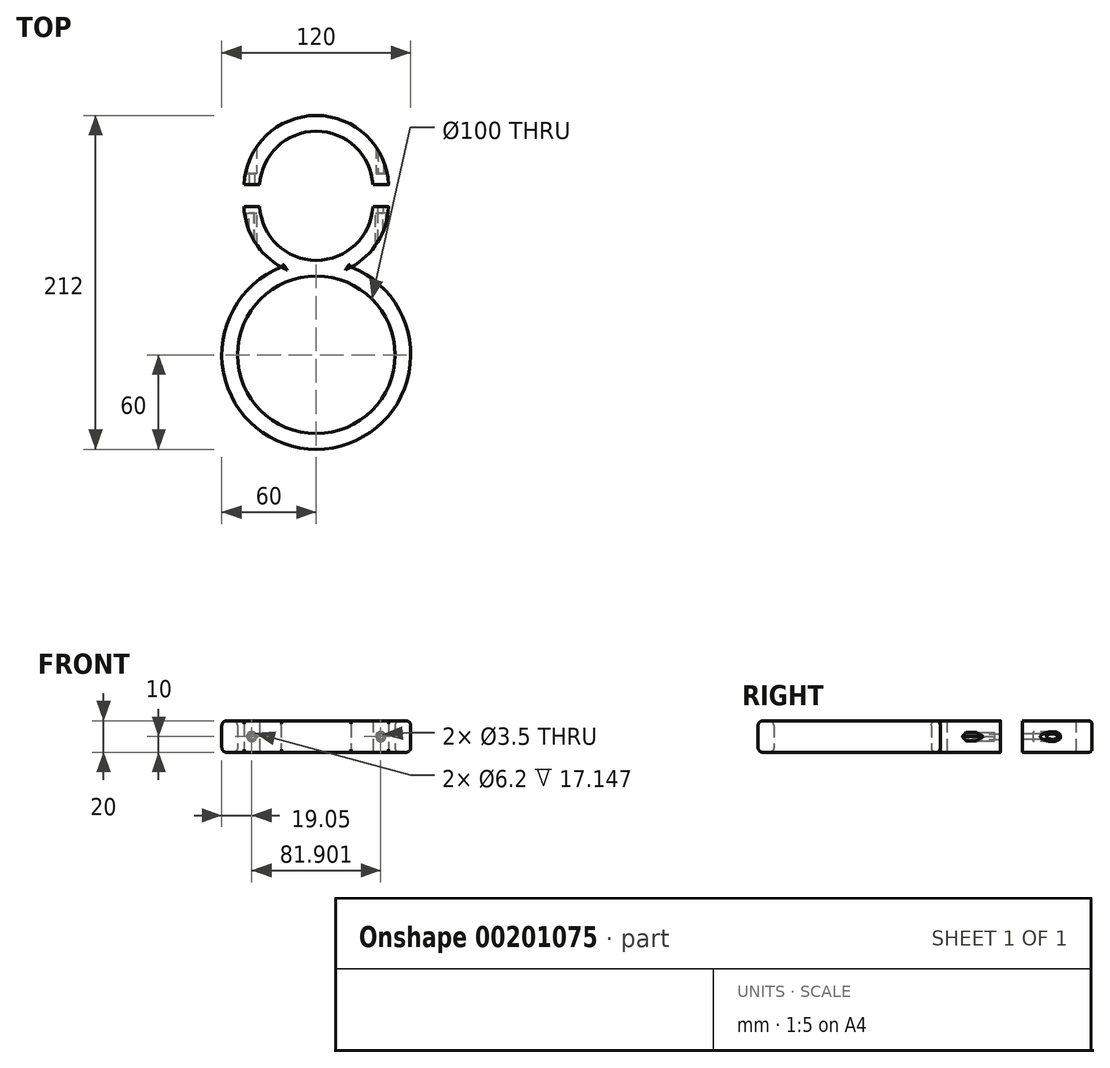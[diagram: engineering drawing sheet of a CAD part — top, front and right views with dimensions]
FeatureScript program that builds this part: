
annotation { "Feature Type Name" : "Feature", "Feature Type Description" : "" }
export const myFeature = defineFeature(function(context is Context, id is Id, definition is map)
    precondition{}
    {
        {
            var Q0;
            Q0=qCreatedBy(makeId("Top.planeOp"),FACE);
            var sketch = newSketch(context, id + "F0", { "sketchPlane" : qUnion([Q0])});
            skCircle(sketch, "E0", {"center": v(0, 0) * mm, "radius": 50 * mm});
            skCircle(sketch, "E1", {"center": v(0, 0) * mm, "radius": 60 * mm});
            skArc(sketch, "E2", {"start": v(-46, 96) * mm, "mid": v(0, 50) * mm, "end": v(46, 96) * mm});
            skArc(sketch, "E3", {"start": v(-36, 96) * mm, "mid": v(0, 60) * mm, "end": v(36, 96) * mm});
            skLineSegment(sketch, "E4", {"start": v(36, 96) * mm, "end": v(46, 96) * mm});
            skLineSegment(sketch, "E5", {"start": v(-36, 96) * mm, "end": v(-46, 96) * mm});
            skArc(sketch, "E6", {"start": v(46, 106) * mm, "mid": v(0, 152) * mm, "end": v(-46, 106) * mm});
            skArc(sketch, "E7", {"start": v(36, 106) * mm, "mid": v(0, 142) * mm, "end": v(-36, 106) * mm});
            skLineSegment(sketch, "E8", {"start": v(-36, 106) * mm, "end": v(-46, 106) * mm});
            skLineSegment(sketch, "E9", {"start": v(36, 106) * mm, "end": v(46, 106) * mm});
            skLineSegment(sketch, "E10", {"start": v(-45.96, 94) * mm, "end": v(-35.94, 94) * mm});
            skLineSegment(sketch, "E11", {"start": v(-45.96, 108) * mm, "end": v(-35.94, 108) * mm});
            skLineSegment(sketch, "E12.MirrorCS", {"start": v(45.96, 94) * mm, "end": v(35.94, 94) * mm});
            skLineSegment(sketch, "E13.MirrorCS", {"start": v(45.96, 108) * mm, "end": v(35.94, 108) * mm});
            skSolve(sketch);
        }
        {
            var Q0;
            {var subQ0=sQuery(id+"F0.wireOp",EDGE,"E1");var subQ1=makeQuery(id+"F0.imprint","INTERSECT",VERTEX,{"derivedFrom":[subQ0,sQuery(id+"F0.wireOp",EDGE,"E3")]});Q0=makeQuery(id+"F0.imprint","IMPRINT",FACE,{"disambiguationData":[TD([[makeQuery(id+"F0.imprint","IMPRINT",EDGE,{"disambiguationData":[TD([[subQ1,1.0]])],"derivedFrom":subQ0}),1.0]])]});}
            var Q1;
            {var subQ0=sQuery(id+"F0.wireOp",EDGE,"E0");Q1=makeQuery(id+"F0.imprint","IMPRINT",FACE,{"disambiguationData":[TD([[makeQuery(id+"F0.imprint","IMPRINT",EDGE,{"derivedFrom":subQ0}),-1.0]])]});}
            var Q2;
            {var subQ5=sQuery(id+"F0.wireOp",EDGE,"E12.MirrorCS");Q2=makeQuery(id+"F0.imprint","IMPRINT",FACE,{"disambiguationData":[TD([[makeQuery(id+"F0.imprint","IMPRINT",EDGE,{"derivedFrom":subQ5}),1.0]])]});}
            var Q3;
            {var subQ5=sQuery(id+"F0.wireOp",EDGE,"E10");Q3=makeQuery(id+"F0.imprint","IMPRINT",FACE,{"disambiguationData":[TD([[makeQuery(id+"F0.imprint","IMPRINT",EDGE,{"derivedFrom":subQ5}),-1.0]])]});}
            var Q4;
            {var subQ0=sQuery(id+"F0.wireOp",EDGE,"E11");Q4=makeQuery(id+"F0.imprint","IMPRINT",FACE,{"disambiguationData":[TD([[makeQuery(id+"F0.imprint","IMPRINT",EDGE,{"derivedFrom":subQ0}),1.0]])]});}
            extrude(context, id + "F1", {"entities" : qUnion([Q0, Q1, Q2, Q3, Q4]), "depth" : 20 * mm, "offsetDistance" : 25 * mm});
        }
        {
            var Q0;
            Q0=makeQuery(id+"F1.opExtrude","SWEPT_FACE",FACE,{"disambiguationData":[OSD([sQuery(id+"F0.wireOp",EDGE,"E12.MirrorCS")])]});
            var sketch = newSketch(context, id + "F2", { "sketchPlane" : qUnion([Q0])});
            skLineSegment(sketch, "E14", {"start": v(-45.96, 10) * mm, "end": v(-35.94, 10) * mm, "construction": true});
            skLineSegment(sketch, "E15", {"start": v(-40.95, 20) * mm, "end": v(-40.95, 0) * mm, "construction": true});
            skCircle(sketch, "E16", {"center": v(-40.95, 10) * mm, "radius": 1.75 * mm});
            skCircle(sketch, "E17.cCircle", {"center": v(-40.95, 10) * mm, "radius": 2.77 * mm, "construction": true});
            skLineSegment(sketch, "E17.0", {"start": v(-39.35, 7.23) * mm, "end": v(-42.55, 7.23) * mm});
            skLineSegment(sketch, "E17.1", {"start": v(-42.55, 7.23) * mm, "end": v(-44.15, 10) * mm});
            skLineSegment(sketch, "E17.2", {"start": v(-44.15, 10) * mm, "end": v(-42.55, 12.77) * mm});
            skLineSegment(sketch, "E17.3", {"start": v(-42.55, 12.77) * mm, "end": v(-39.35, 12.77) * mm});
            skLineSegment(sketch, "E17.4", {"start": v(-39.35, 12.77) * mm, "end": v(-37.75, 10) * mm});
            skLineSegment(sketch, "E17.5", {"start": v(-37.75, 10) * mm, "end": v(-39.35, 7.23) * mm});
            skPoint(sketch, "E17.0.midPoint", {"position": v(-40.95, 7.23) * mm});
            skCircle(sketch, "E18.MirrorC", {"center": v(40.95, 10) * mm, "radius": 2.77 * mm, "construction": true});
            skLineSegment(sketch, "E19.MirrorCS", {"start": v(39.35, 12.77) * mm, "end": v(37.75, 10) * mm});
            skLineSegment(sketch, "E20.MirrorCS", {"start": v(42.55, 7.23) * mm, "end": v(44.15, 10) * mm});
            skLineSegment(sketch, "E21.MirrorCS", {"start": v(39.35, 7.23) * mm, "end": v(42.55, 7.23) * mm});
            skLineSegment(sketch, "E22.MirrorCS", {"start": v(37.75, 10) * mm, "end": v(39.35, 7.23) * mm});
            skPoint(sketch, "E23.MirrorP", {"position": v(40.95, 7.23) * mm});
            skLineSegment(sketch, "E24.MirrorCS", {"start": v(42.55, 12.77) * mm, "end": v(39.35, 12.77) * mm});
            skCircle(sketch, "E25.MirrorC", {"center": v(40.95, 10) * mm, "radius": 1.75 * mm});
            skLineSegment(sketch, "E26.MirrorCS", {"start": v(44.15, 10) * mm, "end": v(42.55, 12.77) * mm});
            skSolve(sketch);
        }
        {
            var Q0;
            Q0=makeQuery(id+"F2.imprint","IMPRINT",FACE,{"disambiguationData":[TD([[makeQuery(id+"F2.imprint","IMPRINT",EDGE,{"derivedFrom":sQuery(id+"F2.wireOp",EDGE,"E16")}),1.0]])]});
            var Q1;
            Q1=makeQuery(id+"F2.imprint","IMPRINT",FACE,{"disambiguationData":[TD([[makeQuery(id+"F2.imprint","IMPRINT",EDGE,{"derivedFrom":sQuery(id+"F2.wireOp",EDGE,"E25.MirrorC")}),-1.0]])]});
            extrude(context, id + "F3", {"entities" : qUnion([Q0, Q1]), "operationType" : NewBodyOperationType.REMOVE, "oppositeDirection" : true, "depth" : 23.9 * mm, "offsetDistance" : 25 * mm});
        }
        {
            var Q0;
            Q0=makeQuery(id+"F2.imprint","IMPRINT",FACE,{"disambiguationData":[TD([[makeQuery(id+"F2.imprint","IMPRINT",EDGE,{"derivedFrom":sQuery(id+"F2.wireOp",EDGE,"E16")}),-1.0]])]});
            var Q1;
            Q1=makeQuery(id+"F2.imprint","IMPRINT",FACE,{"disambiguationData":[TD([[makeQuery(id+"F2.imprint","IMPRINT",EDGE,{"derivedFrom":sQuery(id+"F2.wireOp",EDGE,"E20.MirrorCS")}),1.0]])]});
            extrude(context, id + "F4", {"entities" : qUnion([Q0, Q1]), "operationType" : NewBodyOperationType.REMOVE, "oppositeDirection" : true, "depth" : 25 * mm, "offsetDistance" : 25 * mm});
        }
        {
            var Q0;
            Q0=makeQuery(id+"F2.imprint","IMPRINT",FACE,{"disambiguationData":[TD([[makeQuery(id+"F2.imprint","IMPRINT",EDGE,{"derivedFrom":sQuery(id+"F2.wireOp",EDGE,"E16")}),-1.0]])]});
            var Q1;
            Q1=makeQuery(id+"F2.imprint","IMPRINT",FACE,{"disambiguationData":[TD([[makeQuery(id+"F2.imprint","IMPRINT",EDGE,{"derivedFrom":sQuery(id+"F2.wireOp",EDGE,"E20.MirrorCS")}),1.0]])]});
            extrude(context, id + "F5", {"entities" : qUnion([Q0, Q1]), "operationType" : NewBodyOperationType.ADD, "oppositeDirection" : true, "depth" : 4 * mm, "offsetDistance" : 25 * mm});
        }
        {
            var Q0;
            Q0=makeQuery(id+"F1.opExtrude","SWEPT_FACE",FACE,{"disambiguationData":[OSD([sQuery(id+"F0.wireOp",EDGE,"E13.MirrorCS")])]});
            var sketch = newSketch(context, id + "F6", { "sketchPlane" : qUnion([Q0])});
            skLineSegment(sketch, "E27", {"start": v(-45.96, 10) * mm, "end": v(-35.94, 10) * mm, "construction": true});
            skLineSegment(sketch, "E28", {"start": v(-40.95, 20) * mm, "end": v(-40.95, 0) * mm, "construction": true});
            skCircle(sketch, "E29", {"center": v(-40.95, 10) * mm, "radius": 1.75 * mm});
            skCircle(sketch, "E30.cCircle", {"center": v(-40.95, 10) * mm, "radius": 2.68 * mm, "construction": true});
            skLineSegment(sketch, "E30.0", {"start": v(-39.4, 7.32) * mm, "end": v(-42.5, 7.32) * mm});
            skLineSegment(sketch, "E30.1", {"start": v(-42.5, 7.32) * mm, "end": v(-44.05, 10) * mm});
            skLineSegment(sketch, "E30.2", {"start": v(-44.05, 10) * mm, "end": v(-42.5, 12.68) * mm});
            skLineSegment(sketch, "E30.3", {"start": v(-42.5, 12.68) * mm, "end": v(-39.4, 12.68) * mm});
            skLineSegment(sketch, "E30.4", {"start": v(-39.4, 12.68) * mm, "end": v(-37.85, 10) * mm});
            skLineSegment(sketch, "E30.5", {"start": v(-37.85, 10) * mm, "end": v(-39.4, 7.32) * mm});
            skPoint(sketch, "E30.0.midPoint", {"position": v(-40.95, 7.32) * mm});
            skPoint(sketch, "E31.MirrorP", {"position": v(40.95, 10) * mm});
            skLineSegment(sketch, "E32.MirrorCS", {"start": v(42.5, 12.68) * mm, "end": v(39.4, 12.68) * mm});
            skLineSegment(sketch, "E33.MirrorCS", {"start": v(37.85, 10) * mm, "end": v(39.4, 7.32) * mm});
            skCircle(sketch, "E34.MirrorC", {"center": v(40.95, 10) * mm, "radius": 1.75 * mm});
            skLineSegment(sketch, "E35.MirrorCS", {"start": v(44.05, 10) * mm, "end": v(42.5, 12.68) * mm});
            skLineSegment(sketch, "E36.MirrorCS", {"start": v(39.4, 7.32) * mm, "end": v(42.5, 7.32) * mm});
            skLineSegment(sketch, "E37.MirrorCS", {"start": v(39.4, 12.68) * mm, "end": v(37.85, 10) * mm});
            skPoint(sketch, "E38.MirrorP", {"position": v(40.95, 7.32) * mm});
            skCircle(sketch, "E39.MirrorC", {"center": v(40.95, 10) * mm, "radius": 2.68 * mm, "construction": true});
            skLineSegment(sketch, "E40.MirrorCS", {"start": v(42.5, 7.32) * mm, "end": v(44.05, 10) * mm});
            skCircle(sketch, "E41", {"center": v(-40.95, 10) * mm, "radius": 3.1 * mm});
            skCircle(sketch, "E42", {"center": v(40.95, 10) * mm, "radius": 3.1 * mm});
            skSolve(sketch);
        }
        {
            var Q0;
            Q0=makeQuery(id+"F6.imprint","IMPRINT",FACE,{"disambiguationData":[TD([[makeQuery(id+"F6.imprint","IMPRINT",EDGE,{"derivedFrom":sQuery(id+"F6.wireOp",EDGE,"E29")}),1.0]])]});
            var Q1;
            Q1=makeQuery(id+"F6.imprint","IMPRINT",FACE,{"disambiguationData":[TD([[makeQuery(id+"F6.imprint","IMPRINT",EDGE,{"derivedFrom":sQuery(id+"F6.wireOp",EDGE,"E34.MirrorC")}),-1.0]])]});
            extrude(context, id + "F7", {"entities" : qUnion([Q0, Q1]), "operationType" : NewBodyOperationType.REMOVE, "oppositeDirection" : true, "depth" : 25 * mm, "offsetDistance" : 25 * mm});
        }
        {
            var Q0;
            {var subQ0=sQuery(id+"F6.wireOp",EDGE,"E30.4");Q0=makeQuery(id+"F6.imprint","IMPRINT",FACE,{"disambiguationData":[TD([[makeQuery(id+"F6.imprint","IMPRINT",EDGE,{"derivedFrom":subQ0}),1.0]])]});}
            var Q1;
            Q1=makeQuery(id+"F6.imprint","IMPRINT",FACE,{"disambiguationData":[TD([[makeQuery(id+"F6.imprint","IMPRINT",EDGE,{"derivedFrom":sQuery(id+"F6.wireOp",EDGE,"E29")}),-1.0]])]});
            var Q2;
            {var subQ0=sQuery(id+"F6.wireOp",EDGE,"E30.3");Q2=makeQuery(id+"F6.imprint","IMPRINT",FACE,{"disambiguationData":[TD([[makeQuery(id+"F6.imprint","IMPRINT",EDGE,{"derivedFrom":subQ0}),1.0]])]});}
            var Q3;
            {var subQ0=sQuery(id+"F6.wireOp",EDGE,"E30.2");Q3=makeQuery(id+"F6.imprint","IMPRINT",FACE,{"disambiguationData":[TD([[makeQuery(id+"F6.imprint","IMPRINT",EDGE,{"derivedFrom":subQ0}),1.0]])]});}
            var Q4;
            {var subQ0=sQuery(id+"F6.wireOp",EDGE,"E30.1");Q4=makeQuery(id+"F6.imprint","IMPRINT",FACE,{"disambiguationData":[TD([[makeQuery(id+"F6.imprint","IMPRINT",EDGE,{"derivedFrom":subQ0}),1.0]])]});}
            var Q5;
            {var subQ0=sQuery(id+"F6.wireOp",EDGE,"E30.0");Q5=makeQuery(id+"F6.imprint","IMPRINT",FACE,{"disambiguationData":[TD([[makeQuery(id+"F6.imprint","IMPRINT",EDGE,{"derivedFrom":subQ0}),1.0]])]});}
            var Q6;
            {var subQ0=sQuery(id+"F6.wireOp",EDGE,"E30.5");Q6=makeQuery(id+"F6.imprint","IMPRINT",FACE,{"disambiguationData":[TD([[makeQuery(id+"F6.imprint","IMPRINT",EDGE,{"derivedFrom":subQ0}),1.0]])]});}
            var Q7;
            {var subQ0=sQuery(id+"F6.wireOp",EDGE,"E37.MirrorCS");Q7=makeQuery(id+"F6.imprint","IMPRINT",FACE,{"disambiguationData":[TD([[makeQuery(id+"F6.imprint","IMPRINT",EDGE,{"derivedFrom":subQ0}),-1.0]])]});}
            var Q8;
            Q8=makeQuery(id+"F6.imprint","IMPRINT",FACE,{"disambiguationData":[TD([[makeQuery(id+"F6.imprint","IMPRINT",EDGE,{"derivedFrom":sQuery(id+"F6.wireOp",EDGE,"E32.MirrorCS")}),1.0]])]});
            var Q9;
            {var subQ0=sQuery(id+"F6.wireOp",EDGE,"E32.MirrorCS");Q9=makeQuery(id+"F6.imprint","IMPRINT",FACE,{"disambiguationData":[TD([[makeQuery(id+"F6.imprint","IMPRINT",EDGE,{"derivedFrom":subQ0}),-1.0]])]});}
            var Q10;
            {var subQ0=sQuery(id+"F6.wireOp",EDGE,"E35.MirrorCS");Q10=makeQuery(id+"F6.imprint","IMPRINT",FACE,{"disambiguationData":[TD([[makeQuery(id+"F6.imprint","IMPRINT",EDGE,{"derivedFrom":subQ0}),-1.0]])]});}
            var Q11;
            {var subQ0=sQuery(id+"F6.wireOp",EDGE,"E40.MirrorCS");Q11=makeQuery(id+"F6.imprint","IMPRINT",FACE,{"disambiguationData":[TD([[makeQuery(id+"F6.imprint","IMPRINT",EDGE,{"derivedFrom":subQ0}),-1.0]])]});}
            var Q12;
            {var subQ0=sQuery(id+"F6.wireOp",EDGE,"E33.MirrorCS");Q12=makeQuery(id+"F6.imprint","IMPRINT",FACE,{"disambiguationData":[TD([[makeQuery(id+"F6.imprint","IMPRINT",EDGE,{"derivedFrom":subQ0}),-1.0]])]});}
            var Q13;
            {var subQ0=sQuery(id+"F6.wireOp",EDGE,"E36.MirrorCS");Q13=makeQuery(id+"F6.imprint","IMPRINT",FACE,{"disambiguationData":[TD([[makeQuery(id+"F6.imprint","IMPRINT",EDGE,{"derivedFrom":subQ0}),-1.0]])]});}
            extrude(context, id + "F8", {"entities" : qUnion([Q0, Q1, Q2, Q3, Q4, Q5, Q6, Q7, Q8, Q9, Q10, Q11, Q12, Q13]), "operationType" : NewBodyOperationType.REMOVE, "oppositeDirection" : true, "depth" : 25 * mm, "offsetDistance" : 25 * mm});
        }
        {
            var Q0;
            Q0=makeQuery(id+"F6.imprint","IMPRINT",FACE,{"disambiguationData":[TD([[makeQuery(id+"F6.imprint","IMPRINT",EDGE,{"derivedFrom":sQuery(id+"F6.wireOp",EDGE,"E32.MirrorCS")}),1.0]])]});
            var Q1;
            {var subQ0=sQuery(id+"F6.wireOp",EDGE,"E37.MirrorCS");Q1=makeQuery(id+"F6.imprint","IMPRINT",FACE,{"disambiguationData":[TD([[makeQuery(id+"F6.imprint","IMPRINT",EDGE,{"derivedFrom":subQ0}),-1.0]])]});}
            var Q2;
            {var subQ0=sQuery(id+"F6.wireOp",EDGE,"E33.MirrorCS");Q2=makeQuery(id+"F6.imprint","IMPRINT",FACE,{"disambiguationData":[TD([[makeQuery(id+"F6.imprint","IMPRINT",EDGE,{"derivedFrom":subQ0}),-1.0]])]});}
            var Q3;
            {var subQ0=sQuery(id+"F6.wireOp",EDGE,"E36.MirrorCS");Q3=makeQuery(id+"F6.imprint","IMPRINT",FACE,{"disambiguationData":[TD([[makeQuery(id+"F6.imprint","IMPRINT",EDGE,{"derivedFrom":subQ0}),-1.0]])]});}
            var Q4;
            {var subQ0=sQuery(id+"F6.wireOp",EDGE,"E40.MirrorCS");Q4=makeQuery(id+"F6.imprint","IMPRINT",FACE,{"disambiguationData":[TD([[makeQuery(id+"F6.imprint","IMPRINT",EDGE,{"derivedFrom":subQ0}),-1.0]])]});}
            var Q5;
            {var subQ0=sQuery(id+"F6.wireOp",EDGE,"E35.MirrorCS");Q5=makeQuery(id+"F6.imprint","IMPRINT",FACE,{"disambiguationData":[TD([[makeQuery(id+"F6.imprint","IMPRINT",EDGE,{"derivedFrom":subQ0}),-1.0]])]});}
            var Q6;
            {var subQ0=sQuery(id+"F6.wireOp",EDGE,"E32.MirrorCS");Q6=makeQuery(id+"F6.imprint","IMPRINT",FACE,{"disambiguationData":[TD([[makeQuery(id+"F6.imprint","IMPRINT",EDGE,{"derivedFrom":subQ0}),-1.0]])]});}
            var Q7;
            {var subQ0=sQuery(id+"F6.wireOp",EDGE,"E30.4");Q7=makeQuery(id+"F6.imprint","IMPRINT",FACE,{"disambiguationData":[TD([[makeQuery(id+"F6.imprint","IMPRINT",EDGE,{"derivedFrom":subQ0}),1.0]])]});}
            var Q8;
            Q8=makeQuery(id+"F6.imprint","IMPRINT",FACE,{"disambiguationData":[TD([[makeQuery(id+"F6.imprint","IMPRINT",EDGE,{"derivedFrom":sQuery(id+"F6.wireOp",EDGE,"E29")}),-1.0]])]});
            var Q9;
            {var subQ0=sQuery(id+"F6.wireOp",EDGE,"E30.5");Q9=makeQuery(id+"F6.imprint","IMPRINT",FACE,{"disambiguationData":[TD([[makeQuery(id+"F6.imprint","IMPRINT",EDGE,{"derivedFrom":subQ0}),1.0]])]});}
            var Q10;
            {var subQ0=sQuery(id+"F6.wireOp",EDGE,"E30.0");Q10=makeQuery(id+"F6.imprint","IMPRINT",FACE,{"disambiguationData":[TD([[makeQuery(id+"F6.imprint","IMPRINT",EDGE,{"derivedFrom":subQ0}),1.0]])]});}
            var Q11;
            {var subQ0=sQuery(id+"F6.wireOp",EDGE,"E30.1");Q11=makeQuery(id+"F6.imprint","IMPRINT",FACE,{"disambiguationData":[TD([[makeQuery(id+"F6.imprint","IMPRINT",EDGE,{"derivedFrom":subQ0}),1.0]])]});}
            var Q12;
            {var subQ0=sQuery(id+"F6.wireOp",EDGE,"E30.2");Q12=makeQuery(id+"F6.imprint","IMPRINT",FACE,{"disambiguationData":[TD([[makeQuery(id+"F6.imprint","IMPRINT",EDGE,{"derivedFrom":subQ0}),1.0]])]});}
            var Q13;
            {var subQ0=sQuery(id+"F6.wireOp",EDGE,"E30.3");Q13=makeQuery(id+"F6.imprint","IMPRINT",FACE,{"disambiguationData":[TD([[makeQuery(id+"F6.imprint","IMPRINT",EDGE,{"derivedFrom":subQ0}),1.0]])]});}
            extrude(context, id + "F9", {"entities" : qUnion([Q0, Q1, Q2, Q3, Q4, Q5, Q6, Q7, Q8, Q9, Q10, Q11, Q12, Q13]), "operationType" : NewBodyOperationType.ADD, "oppositeDirection" : true, "depth" : 7 * mm, "offsetDistance" : 25 * mm});
        }
        {
            var Q0;
            Q0=makeQuery(id+"F1.opExtrude","CAP_EDGE",EDGE,{"disambiguationData":[OSD([sQuery(id+"F0.wireOp",EDGE,"E1")])],"isStart":false});
            var Q1;
            Q1=makeQuery(id+"F1.opExtrude","CAP_EDGE",EDGE,{"disambiguationData":[OSD([sQuery(id+"F0.wireOp",EDGE,"E0")])],"isStart":false});
            var Q2;
            Q2=makeQuery(id+"F1.opExtrude","CAP_EDGE",EDGE,{"disambiguationData":[OSD([sQuery(id+"F0.wireOp",EDGE,"E1")])],"isStart":true});
            var Q3;
            Q3=makeQuery(id+"F1.opExtrude","CAP_EDGE",EDGE,{"disambiguationData":[OSD([sQuery(id+"F0.wireOp",EDGE,"E0")])],"isStart":true});
            fillet(context, id + "F10", {"entities" : qUnion([Q0, Q1, Q2, Q3]), "tangentPropagation" : true, "radius" : 3 * mm, "defaultsChanged" : false, "vertexSettings" : [], "allowEdgeOverflow" : false});
        }
        {
            var Q0;
            {var subQ0=sQuery(id+"F0.wireOp",EDGE,"E2");Q0=makeQuery(id+"F1.opExtrude","CAP_EDGE",EDGE,{"disambiguationData":[OSD([subQ0]),TDD([makeQuery(id+"F0.imprint","IMPRINT",EDGE,{"disambiguationData":[TD([[makeQuery(id+"F0.imprint","INTERSECT",VERTEX,{"derivedFrom":[subQ0,sQuery(id+"F0.wireOp",EDGE,"E10")]}),-1.0]])],"derivedFrom":subQ0})])],"isStart":false});}
            var Q1;
            {var subQ0=sQuery(id+"F0.wireOp",EDGE,"E2");Q1=makeQuery(id+"F1.opExtrude","CAP_EDGE",EDGE,{"disambiguationData":[OSD([subQ0]),TDD([makeQuery(id+"F0.imprint","IMPRINT",EDGE,{"disambiguationData":[TD([[makeQuery(id+"F0.imprint","INTERSECT",VERTEX,{"derivedFrom":[subQ0,sQuery(id+"F0.wireOp",EDGE,"E12.MirrorCS")]}),1.0]])],"derivedFrom":subQ0})])],"isStart":false});}
            var Q2;
            Q2=makeQuery(id+"F1.opExtrude","CAP_EDGE",EDGE,{"disambiguationData":[OSD([sQuery(id+"F0.wireOp",EDGE,"E6")])],"isStart":false});
            var Q3;
            Q3=makeQuery(id+"F1.opExtrude","CAP_EDGE",EDGE,{"disambiguationData":[OSD([sQuery(id+"F0.wireOp",EDGE,"E6")])],"isStart":true});
            var Q4;
            {var subQ0=sQuery(id+"F0.wireOp",EDGE,"E2");Q4=makeQuery(id+"F1.opExtrude","CAP_EDGE",EDGE,{"disambiguationData":[OSD([subQ0]),TDD([makeQuery(id+"F0.imprint","IMPRINT",EDGE,{"disambiguationData":[TD([[makeQuery(id+"F0.imprint","INTERSECT",VERTEX,{"derivedFrom":[subQ0,sQuery(id+"F0.wireOp",EDGE,"E12.MirrorCS")]}),1.0]])],"derivedFrom":subQ0})])],"isStart":true});}
            var Q5;
            {var subQ0=sQuery(id+"F0.wireOp",EDGE,"E2");Q5=makeQuery(id+"F1.opExtrude","CAP_EDGE",EDGE,{"disambiguationData":[OSD([subQ0]),TDD([makeQuery(id+"F0.imprint","IMPRINT",EDGE,{"disambiguationData":[TD([[makeQuery(id+"F0.imprint","INTERSECT",VERTEX,{"derivedFrom":[subQ0,sQuery(id+"F0.wireOp",EDGE,"E10")]}),-1.0]])],"derivedFrom":subQ0})])],"isStart":true});}
            fillet(context, id + "F11", {"entities" : qUnion([Q0, Q1, Q2, Q3, Q4, Q5]), "tangentPropagation" : true, "radius" : 2 * mm, "defaultsChanged" : true, "vertexSettings" : [], "allowEdgeOverflow" : false});
        }
    });
